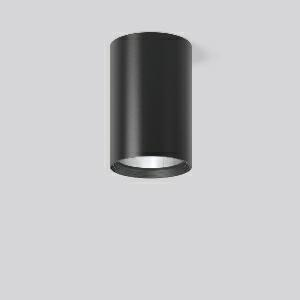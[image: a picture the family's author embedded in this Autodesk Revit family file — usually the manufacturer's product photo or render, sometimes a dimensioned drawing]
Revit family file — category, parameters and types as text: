
# Revit family: heledon_maxi_a_931239_003_76_6bca
name_source: partatom
category: Lighting Fixtures
units: mm (PartAtom-declared; Revit-internal decimal feet)

## family parameters
Cut with Voids When Loaded = No
Host = Face
Light Source = No
Part Type = Normal
Room Calculation Point = No
Round Connector Dimension = Use Diameter
Shared = No

## types (1)
- HELEDON maxi A (1 x LED Modul 920 meat+, 2250 lm, 2000)
    Apparent Load = 33 VA
    Approval mark = CE
    CIE Flux Codes = 100 100 100 100 100
    Color Rendering = 90
    Color Temperature = 2000
    Default Elevation = 1800 mm
    Description = Series: HELEDON maxi
Cylindrical surface-mounted downlight. Housing: die-cast aluminium, powder-coated. Internal ceiling frame polycarbonate with bayonet mounting. Black plastic ring and recessed LED to prevent glare from the side. Optical assembly with reflector made of MIRO-Silver with 98% total light reflection for outstanding efficiency - can be changed without tools. Special LED for illumination of meat included. Suitable for Ceiling mounting. Easy installation with a separate ceiling frame with bayonet mounting and plug connection. Driver integrated. Connected via plug-in connector. High quality converter without flickering and stroboscopic effect. The following accessories can be mounted without use of tools: interchangeable lenses, decorative glasses, honeycomb louvre, clear and frosted diffusers, white interchangeable plastic ring. 
Colour: deep black, matt (RAL 9005)
Diameter: 123 mm
Height: 183 mm
Lamp: LED
Socket: without socket
Colour temperature: meat +
System power: 33 W
Rated luminous flux: 2250 lm
Luminous efficiency: 68 lm/W
Control gear: Converter, dimmable, DALI
Protection class: I
Type of protection: IP 20
    Height = 183 mm
    Lamp = 1 x LED Modul 920 meat+
    Lamp Light Flux = 2250 lm
    Lamp count = 1
    Length = 123 mm
    Lifetime = 50000 h
    Luminous efficacy = 68 lm/W
    Manufacturer = RZB
    ModVariant = No
    Model = 931239.003.76
    Mounting Place = Ceiling
    Mounting Type = Surface mounted
    Number of Poles = 1
    OnlyDefault = Yes
    Power Factor = 1
    Product Name = HELEDON maxi A
    Product group = Surface mounted downlights
    ProductGroupID = 302
    Protection Class = Protection class I
    Protection Degree = IP 20
    RLX_Detail_Level = 1
    RLX_Emergency_Light_Flux = 0 lm
    RLX_Emergency_Type = 0
    RLX_Emergency_Type_DB = No
    RlxData = <blob elided: 98789 chars, md5=805945e6>
    Socket = socket
    Standby Power = 0 W
    System Light Flux = 2250 lm
    System Power = 33 W
    Type Comments = Product without accessories
    Type Image = 931192.003.jpg
    URL = http://relux.com
    VarID = ---
    Voltage = 230 V
    Voltage Range = 220-240 V
    Weight = 0.00 kg
    Width = 0 mm  [stored 0 ft]

note: [stored X ft] marks values corroborated as IEEE doubles in the binary element streams (Revit-internal decimal feet)

## geometry (parser evidence)
native form markers: Blend x4, Sweep x10
no freeform markers — native parametric forms only
